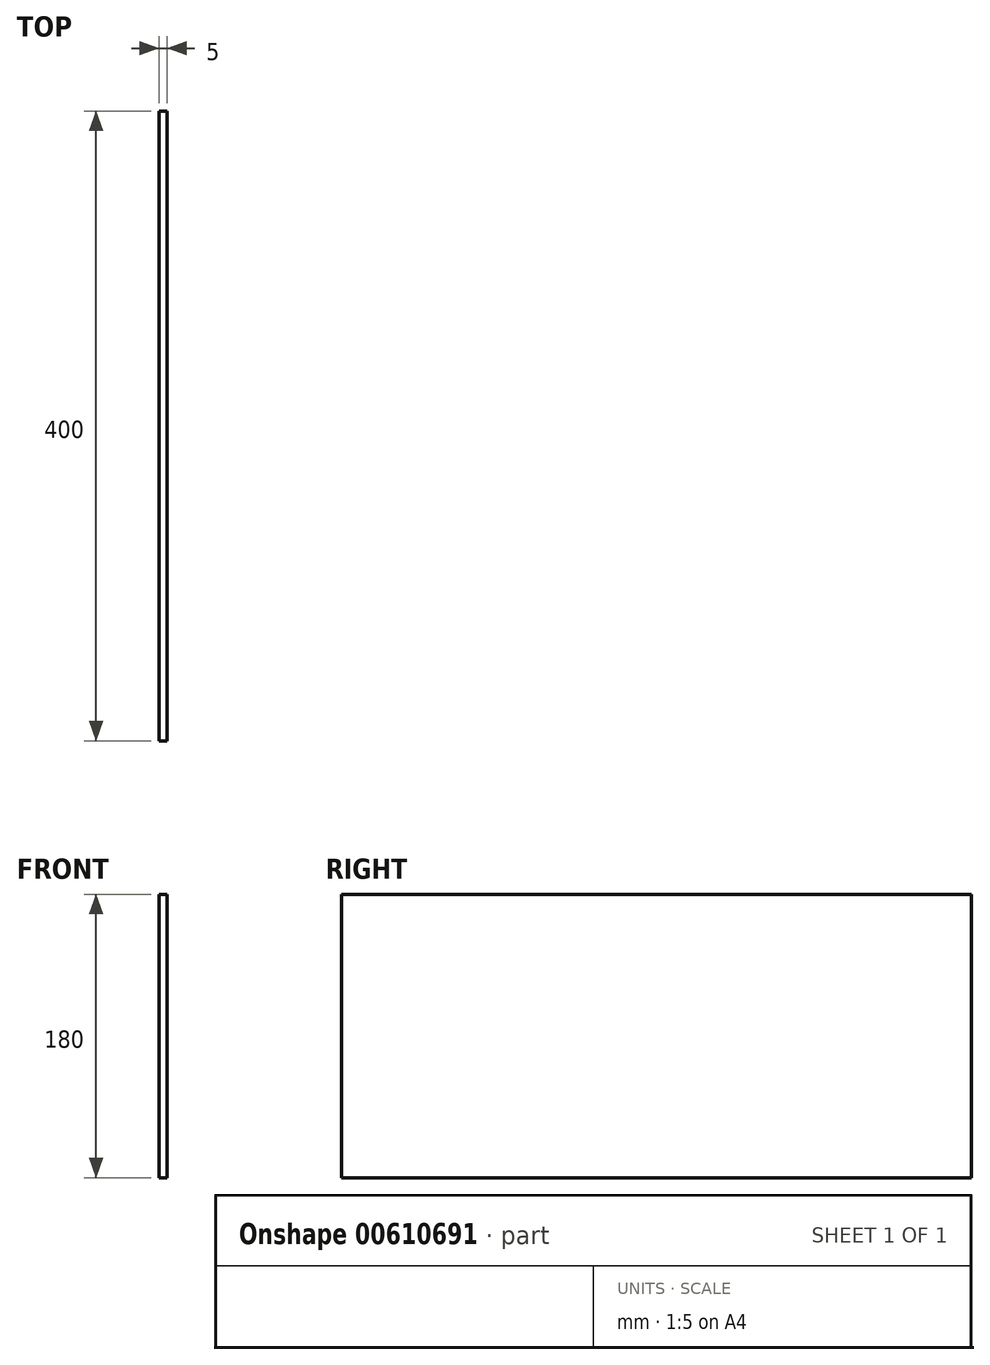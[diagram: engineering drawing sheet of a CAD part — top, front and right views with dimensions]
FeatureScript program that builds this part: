
annotation { "Feature Type Name" : "Feature", "Feature Type Description" : "" }
export const myFeature = defineFeature(function(context is Context, id is Id, definition is map)
    precondition{}
    {
        {
            var Q0;
            Q0=qCreatedBy(makeId("Right.planeOp"),FACE);
            var sketch = newSketch(context, id + "F0", { "sketchPlane" : qUnion([Q0])});
            skLineSegment(sketch, "E0.bottom", {"start": v(0, 0) * mm, "end": v(400, 0) * mm});
            skLineSegment(sketch, "E0.top", {"start": v(0, 180) * mm, "end": v(400, 180) * mm});
            skLineSegment(sketch, "E0.left", {"start": v(0, 0) * mm, "end": v(0, 180) * mm});
            skLineSegment(sketch, "E0.right", {"start": v(400, 0) * mm, "end": v(400, 180) * mm});
            skSolve(sketch);
        }
        {
            var Q0;
            Q0 = qSketchRegion(id + "F0", true);
            extrude(context, id + "F1", {"entities" : qUnion([Q0]), "depth" : 5 * mm, "offsetDistance" : 25 * mm});
        }
    });
